# Revit family: OmegaFlex-TracPipe-Regulator_2PSI
name_source: partatom
category: Pipe Accessories
units: mm (PartAtom-declared; Revit-internal decimal feet)

## family parameters
Always vertical = No
Classification Number = 23.60.30.11.17
Cut with Voids When Loaded = No
Part Type = Valve - Breaks Into
Round Connector Dimension = Use Radius
Shared = No
Work Plane-Based = No

## types (11) — shared parameters
Description = See Part Description
Manufacturer = OmegaFlex
Model = TracPipe CounterStrike
URL = https://www.omegaflex.com

## per-type parameters (varying)
| type | Default Elevation | Dimension B | Dimension C | Dimension D | Height | Offset to CL Connection | Regulator Type | Upper Control Diameter | Upper Control Diameter 1 | Upper Control Diameter 2 | Upper Diaphragm Diameter |
| 0-1/2" NPT - 8" W.C. | 0 " | 4 " | 0.5 " | 4.375 " | 3.5 " | 0.7 " | 1 | 0.5 " | 0.364 " | 0.239 " | 1.2 " |
| 0-1/2" NPT - 11" W.C. | 1.4 " | 4 " | 0.5 " | 4.375 " | 3.5 " | 0.7 " | 2 | 0.5 " | 0.364 " | 0.239 " | 1.2 " |
| 0-3/4" NPT - 8" W.C. | 1.641 " | 4.688 " | 0.75 " | 6 " | 5.02 " | 1.05 " | 3 | 0.586 " | 0.426 " | 0.301 " | 1.406 " |
| 0-3/4" NPT - 11" W.C. | 1.641 " | 4.688 " | 0.75 " | 6 " | 5.02 " | 1.05 " | 4 | 0.586 " | 0.426 " | 0.301 " | 1.406 " |
| 1" NPT - 8" W.C. | 1.324 " | 3.782 " | 1 " | 4.092 " | 5.59 " | 1.4 " | 5 | 0.473 " | 0.344 " | 0.219 " | 1.135 " |
| 0-1/2" NPT - HC | 1.4 " | 4.49 " | 0.5 " | 4.72 " | 6.89 " | 0.7 " | 6 | 0.561 " | 0.408 " | 0.283 " | 1.347 " |
| 0-3/4" NPT - HC | 1.4 " | 4.49 " | 0.75 " | 4.72 " | 6.89 " | 1.05 " | 7 | 0.561 " | 0.408 " | 0.283 " | 1.347 " |
| 1" NPT - HC | 1.4 " | 4.49 " | 1 " | 4.72 " | 6.89 " | 1.4 " | 8 | 0.561 " | 0.408 " | 0.283 " | 1.347 " |
| 1-1/4" NPT - HC | 1.4 " | 7.56 " | 1.25 " | 7.68 " | 10 " | 1.75 " | 9 | 0.945 " | 0.687 " | 0.562 " | 2.268 " |
| 1-1/2" NPT - HC | 1.4 " | 7.56 " | 1.5 " | 7.68 " | 10 " | 2.1 " | 10 | 0.945 " | 0.687 " | 0.562 " | 2.268 " |
| 2" NPT - HC | 1.4 " | 7.56 " | 2 " | 9.29 " | 12.44 " | 2.8 " | 11 | 0.945 " | 0.687 " | 0.562 " | 2.268 " |

## geometry (parser evidence)
native form markers: Sweep x2
no freeform markers — native parametric forms only
